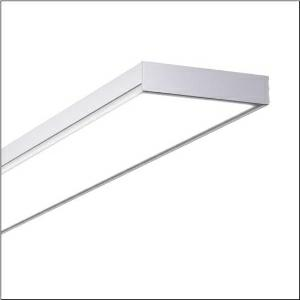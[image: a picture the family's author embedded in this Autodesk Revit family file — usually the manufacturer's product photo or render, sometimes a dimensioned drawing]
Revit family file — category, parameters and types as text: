
# Revit family: apollon_r__31_surface_51mp26wm2441ea_9a05
name_source: partatom
category: Lighting Fixtures
units: mm (PartAtom-declared; Revit-internal decimal feet)

## family parameters
Cut with Voids When Loaded = No
Host = Face
Light Source = No
Part Type = Normal
Room Calculation Point = No
Round Connector Dimension = Use Diameter
Shared = No

## types (1)
- Apollon® 31 Surface (1 x LED, 4600 lm, 33 W, 4000K)
    Apparent Load = 33 VA
    CIE Flux Codes = 61 87 97 97 100
    Color Rendering = 80
    Color Temperature = 4000K
    Default Elevation = 1800 mm
    Description = Apollon® 31 Surface, office luminaire, primary optical cover: micro prismatic cover, of PMMA, light emission: direct distribution, primary light characteristic: symmetric, installation type: surface-mounted, LED, rated luminous flux: 4.600lm, luminous efficacy: 139lm/W, light colour: 840, colour temperature: 4000K, control gear: ON/OFF Multilumen, with terminal, 3-pole, mains connection: 220..240V, AC, 50/60Hz, rated input power: 33W, housing, of sheet steel, coil coated, metallic grey (RAL 9006), length: 1.545mm, width: 200mm, height: 44mm, protection rating (complete): IP20, insulation class (complete): insulation class II (safety insulation), certification: CE, impact resistance: IK02, permissible operating ambient temperature: -20..+40°C, packaging unit: 1 piece
    Height = 44 mm
    Lamp = 1 x LED
    Lamp Light Flux = 4600 lm
    Lamp Power = 33 W
    Lamp count = 1
    Length = 1545 mm
    Luminous efficacy = 139 lm/W
    Manufacturer = Siteco
    ModVariant = No
    Model = 51MP26WM2441EA
    Mounting Place = Ceiling
    Mounting Type = Surface mounted
    Number of Poles = 1
    OnlyDefault = Yes
    Power Factor = 1
    Product Name = Apollon® 31 Surface
    Product group = office luminaire | ceiling mounted
    ProductGroupID = 303
    Protection Class = Protection class II
    Protection Degree = IP 20
    RLX_Detail_Level = 1
    RLX_Emergency_Light_Flux = 0 lm
    RLX_Emergency_Type = 0
    RLX_Emergency_Type_DB = No
    RlxData = <blob elided: 24101 chars, md5=6b9de1dd>
    Socket = socket
    Standby Power = 0 W
    System Light Flux = 4600 lm
    System Power = 33 W
    Type Comments = Product without accessories
    Type Image = l_1313654.jpg
    URL = http://relux.com
    VarID = ---
    Voltage = 0 V
    Weight = 0.00 kg
    Width = 200 mm

## geometry (parser evidence)
native form markers: Blend x4, Sweep x11
no freeform markers — native parametric forms only
